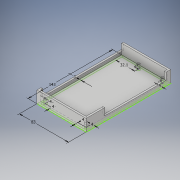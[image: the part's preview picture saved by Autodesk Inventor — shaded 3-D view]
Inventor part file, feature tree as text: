
AUTODESK INVENTOR PART (.ipt)
format: ipt  version: 2019.1 (Build 231200000, 200)  size: 166,912 bytes
history: native  units: in
note: dims shown in document units (in); Inventor stores cm internally (conversion verified against a paired STEP export)
features: extrude x7, sketch x2, hole x1
ambient origin geometry x8: Origin, YZ Plane, XZ Plane, XY Plane, X Axis, Y Axis, Z Axis, Center Point
bodies: Solid1 (feature_tree)
feature tree (10):
  sketch  "Sketch1"  dims[d0=5.6299in d1=3.2677in]
  extrude  "Floor"  Depth=3.2677in
  extrude  "Walls"  Depth=0.1181in TaperAngle=0.0deg
  sketch  "Sketch2"  dims[d2=0.1181in d20=0.1181in d21=0.0in d24=0.7874in d25=0.0in d30=0.1575in d31=0.1575in d32=0.1575in d33=0.1575in d34=0.1575in d35=0.1575in d36=0.1575in d37=1.2638in d42=0.315in d43=0.0in d44=0.1181in d45=0.2362in d46=0.1575in d47=0.0787in d48=90.0deg d49=0.315in d50=0.0in d51=0.7874in d52=0.0in d53=0.7874in d54=0.0in d55=0.315in d56=0.0in d57=0.315in d58=0.0in d59=0.0394in d60=0.0394in d61=0.0394in d62=0.0059in d63=0.0098in d64=0.0148in d65=0.5635in d66=0.0295in d67=0.8108in d68=0.0025in d69=0.0295in d70=0.0148in]
  extrude  "mounts"  Depth=0.7874in TaperAngle=0.0deg
  hole  "Hole1"  [1 undecoded]
  extrude  "Extrusion5"  Depth=0.315in
  extrude  "Extrusion6"  Depth=0.315in
  extrude  "Extrusion7"  Depth=0.315in
  extrude  "Extrusion8"  Depth=0.315in
note: 1 required parameter value undecoded (feature->parameter linkage not recoverable at this tier; creation-order binding heuristic only, values carry confidence <= 0.55)
